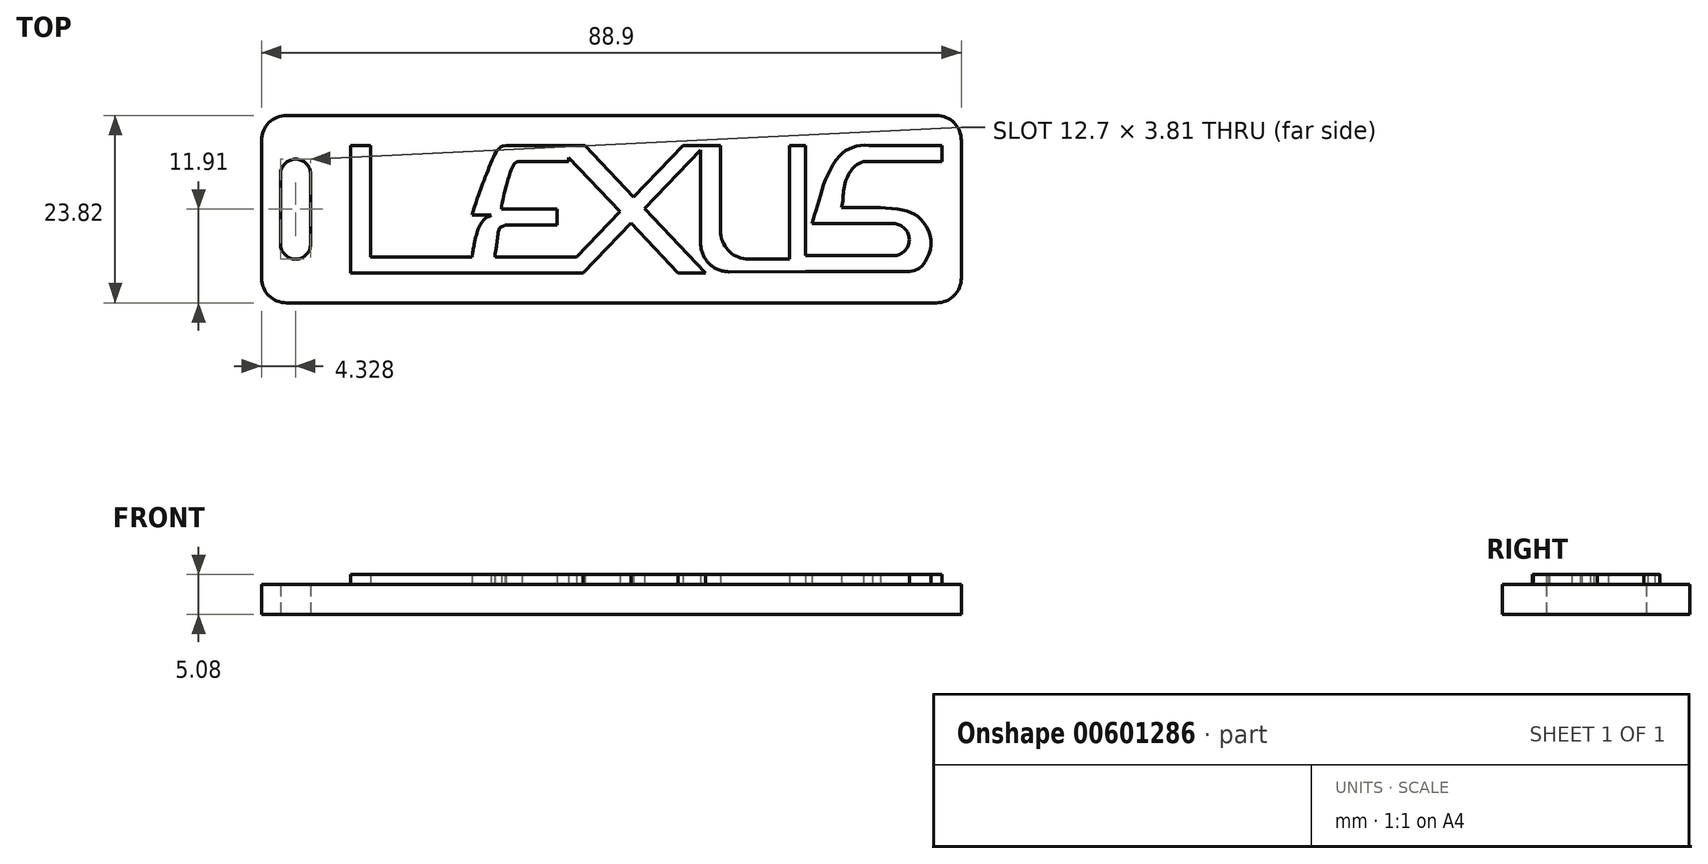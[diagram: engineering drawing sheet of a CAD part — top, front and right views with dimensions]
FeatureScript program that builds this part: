
annotation { "Feature Type Name" : "Feature", "Feature Type Description" : "" }
export const myFeature = defineFeature(function(context is Context, id is Id, definition is map)
    precondition{}
    {
        {
            var Q0;
            Q0=qCreatedBy(makeId("Top.planeOp"),FACE);
            var sketch = newSketch(context, id + "F0", { "sketchPlane" : qUnion([Q0])});
            skLineSegment(sketch, "E0.bottom", {"start": v(41.28, -11.9) * mm, "end": v(-41.28, -11.9) * mm});
            skLineSegment(sketch, "E0.top", {"start": v(41.28, 11.9) * mm, "end": v(-41.28, 11.9) * mm});
            skLineSegment(sketch, "E0.left", {"start": v(44.45, -8.73) * mm, "end": v(44.45, 8.73) * mm});
            skLineSegment(sketch, "E0.right", {"start": v(-44.45, -8.73) * mm, "end": v(-44.45, 8.73) * mm});
            skPoint(sketch, "E0.middle", {"position": v(0, 0) * mm});
            skPoint(sketch, "E1.visualSharp", {"position": v(-44.45, 11.9) * mm});
            skArc(sketch, "E1.filletArc", {"start": v(-41.28, 11.9) * mm, "mid": v(-43.52, 10.98) * mm, "end": v(-44.45, 8.73) * mm});
            skPoint(sketch, "E2.visualSharp", {"position": v(44.45, 11.9) * mm});
            skArc(sketch, "E2.filletArc", {"start": v(44.45, 8.73) * mm, "mid": v(43.52, 10.98) * mm, "end": v(41.28, 11.9) * mm});
            skPoint(sketch, "E3.visualSharp", {"position": v(44.45, -11.9) * mm});
            skArc(sketch, "E3.filletArc", {"start": v(41.28, -11.9) * mm, "mid": v(43.52, -10.98) * mm, "end": v(44.45, -8.73) * mm});
            skPoint(sketch, "E4.visualSharp", {"position": v(-44.45, -11.9) * mm});
            skArc(sketch, "E4.filletArc", {"start": v(-44.45, -8.73) * mm, "mid": v(-43.52, -10.98) * mm, "end": v(-41.28, -11.9) * mm});
            skLineSegment(sketch, "E5.bottom", {"start": v(-40.12, -6.35) * mm, "end": v(-40.12, -6.35) * mm});
            skLineSegment(sketch, "E5.top", {"start": v(-40.12, 6.35) * mm, "end": v(-40.12, 6.35) * mm});
            skLineSegment(sketch, "E5.left", {"start": v(-38.22, -4.45) * mm, "end": v(-38.22, 4.45) * mm});
            skLineSegment(sketch, "E5.right", {"start": v(-42.03, -4.45) * mm, "end": v(-42.03, 4.45) * mm});
            skPoint(sketch, "E5.middle", {"position": v(-40.12, 0) * mm});
            skPoint(sketch, "E6.visualSharp", {"position": v(-38.22, 6.35) * mm});
            skArc(sketch, "E6.filletArc", {"start": v(-38.22, 4.45) * mm, "mid": v(-38.77, 5.8) * mm, "end": v(-40.12, 6.35) * mm});
            skPoint(sketch, "E7.visualSharp", {"position": v(-42.03, 6.35) * mm});
            skArc(sketch, "E7.filletArc", {"start": v(-40.12, 6.35) * mm, "mid": v(-41.47, 5.8) * mm, "end": v(-42.03, 4.45) * mm});
            skPoint(sketch, "E8.visualSharp", {"position": v(-42.03, -6.35) * mm});
            skArc(sketch, "E8.filletArc", {"start": v(-42.03, -4.45) * mm, "mid": v(-41.47, -5.8) * mm, "end": v(-40.12, -6.35) * mm});
            skPoint(sketch, "E9.visualSharp", {"position": v(-38.22, -6.35) * mm});
            skArc(sketch, "E9.filletArc", {"start": v(-40.12, -6.35) * mm, "mid": v(-38.77, -5.8) * mm, "end": v(-38.22, -4.45) * mm});
            skSolve(sketch);
        }
        {
            var Q0;
            Q0=makeQuery(id+"F0.imprint","IMPRINT",FACE,{"disambiguationData":[TD([[makeQuery(id+"F0.imprint","IMPRINT",EDGE,{"derivedFrom":sQuery(id+"F0.wireOp",EDGE,"E0.bottom")}),-1.0]])]});
            extrude(context, id + "F1", {"entities" : qUnion([Q0]), "depth" : 3.8 * mm, "offsetDistance" : 25.4 * mm});
        }
        {
            var Q0;
            Q0=makeQuery(id+"F1.opExtrude","CAP_FACE",FACE,{"disambiguationData":[OSD([sQuery(id+"F0.wireOp",EDGE,"E0.bottom"),sQuery(id+"F0.wireOp",EDGE,"E0.top"),sQuery(id+"F0.wireOp",EDGE,"E0.left"),sQuery(id+"F0.wireOp",EDGE,"E0.right"),sQuery(id+"F0.wireOp",EDGE,"E1.filletArc"),sQuery(id+"F0.wireOp",EDGE,"E2.filletArc"),sQuery(id+"F0.wireOp",EDGE,"E3.filletArc"),sQuery(id+"F0.wireOp",EDGE,"E4.filletArc"),sQuery(id+"F0.wireOp",EDGE,"E5.left"),sQuery(id+"F0.wireOp",EDGE,"E5.right"),sQuery(id+"F0.wireOp",EDGE,"E6.filletArc"),sQuery(id+"F0.wireOp",EDGE,"E7.filletArc"),sQuery(id+"F0.wireOp",EDGE,"E8.filletArc"),sQuery(id+"F0.wireOp",EDGE,"E9.filletArc")])],"isStart":false});
            var sketch = newSketch(context, id + "F2", { "sketchPlane" : qUnion([Q0])});
            skLineSegment(sketch, "E10", {"start": v(-33.14, -8.1) * mm, "end": v(-33.14, 8.1) * mm});
            skLineSegment(sketch, "E11", {"start": v(-33.14, 8.1) * mm, "end": v(-30.6, 8.1) * mm});
            skLineSegment(sketch, "E12", {"start": v(-30.6, 8.1) * mm, "end": v(-30.6, -6.06) * mm});
            skLineSegment(sketch, "E13", {"start": v(-30.6, -6.06) * mm, "end": v(-17.69, -6.06) * mm});
            skLineSegment(sketch, "E14", {"start": v(-14.93, -8.1) * mm, "end": v(-33.14, -8.1) * mm});
            skLineSegment(sketch, "E15", {"start": v(-15.3, -0.76) * mm, "end": v(-17.69, -0.76) * mm});
            skFitSpline(sketch, "E16", {"points": [v(-17.69, -0.76) * mm, v(-16.6, 2.6) * mm, v(-15.9, 4.42) * mm, v(-15, 6.56) * mm, v(-14.35, 7.63) * mm, v(-13.4, 8.1) * mm], "startDerivative": vector(6.68, 22.76) * mm, "endDerivative": vector(10.34, 0.39) * mm});
            skLineSegment(sketch, "E17", {"start": v(-13.4, 8.1) * mm, "end": v(-5.41, 8.1) * mm});
            skLineSegment(sketch, "E18", {"start": v(-5.41, 8.1) * mm, "end": v(-5.41, 6.06) * mm});
            skLineSegment(sketch, "E19", {"start": v(-5.41, 6.06) * mm, "end": v(-11.37, 6.06) * mm});
            skLineSegment(sketch, "E20", {"start": v(-13.98, 0) * mm, "end": v(-6.88, 0) * mm});
            skLineSegment(sketch, "E21", {"start": v(-6.88, 0) * mm, "end": v(-6.88, -2.03) * mm});
            skLineSegment(sketch, "E22", {"start": v(-6.88, -2.03) * mm, "end": v(-13.51, -2.03) * mm});
            skFitSpline(sketch, "E23", {"points": [v(-11.37, 6.06) * mm, v(-12.28, 5.85) * mm, v(-12.92, 4.45) * mm, v(-13.37, 2.93) * mm, v(-13.98, 0) * mm], "startDerivative": vector(-6.84, 0.48) * mm, "endDerivative": vector(-1.14, -9.07) * mm});
            skFitSpline(sketch, "E24", {"points": [v(-17.69, -6.06) * mm, v(-17.48, -4.75) * mm, v(-17.16, -3.28) * mm, v(-16.77, -2.16) * mm, v(-16.14, -1.27) * mm, v(-15.3, -0.76) * mm], "startDerivative": vector(1.78, 14.07) * mm, "endDerivative": vector(7.84, 3.88) * mm});
            skFitSpline(sketch, "E25", {"points": [v(-13.51, -2.03) * mm, v(-14.2, -2.4) * mm, v(-14.5, -3.96) * mm, v(-14.71, -5.37) * mm, v(-14.77, -6.06) * mm], "startDerivative": vector(-4.95, -2.36) * mm, "endDerivative": vector(0.17, -4.54) * mm});
            skLineSegment(sketch, "E26", {"start": v(-14.93, -8.1) * mm, "end": v(-4.44, -8.1) * mm});
            skLineSegment(sketch, "E27", {"start": v(-4.44, -8.1) * mm, "end": v(-4.44, -6.06) * mm});
            skLineSegment(sketch, "E28", {"start": v(-4.44, -6.06) * mm, "end": v(-14.77, -6.06) * mm});
            skLineSegment(sketch, "E29", {"start": v(37.84, -7.94) * mm, "end": v(24.67, -7.94) * mm});
            skLineSegment(sketch, "E30", {"start": v(24.67, -5.9) * mm, "end": v(35.8, -5.9) * mm});
            skLineSegment(sketch, "E31", {"start": v(37.84, -3.88) * mm, "end": v(37.84, -3.88) * mm});
            skLineSegment(sketch, "E32", {"start": v(35.8, -1.84) * mm, "end": v(25.48, -1.84) * mm});
            skPoint(sketch, "E33.visualSharp", {"position": v(37.84, -1.84) * mm});
            skArc(sketch, "E33.filletArc", {"start": v(37.84, -3.88) * mm, "mid": v(37.24, -2.44) * mm, "end": v(35.8, -1.84) * mm});
            skPoint(sketch, "E34.visualSharp", {"position": v(37.84, -5.9) * mm});
            skArc(sketch, "E34.filletArc", {"start": v(35.8, -5.9) * mm, "mid": v(37.24, -5.31) * mm, "end": v(37.84, -3.88) * mm});
            skFitSpline(sketch, "E35", {"points": [v(37.84, -7.94) * mm, v(39.4, -7.3) * mm, v(40.12, -6.12) * mm, v(40.58, -4.82) * mm, v(40.45, -3.13) * mm, v(39.67, -1.7) * mm, v(38.76, -0.8) * mm, v(37.84, -0.34) * mm, v(36.42, 0) * mm, v(34.18, 0.19) * mm], "startDerivative": vector(16.67, 3.29) * mm, "endDerivative": vector(-12.35, -0.23) * mm});
            skLineSegment(sketch, "E36", {"start": v(34.18, 0.19) * mm, "end": v(29.24, 0.19) * mm});
            skFitSpline(sketch, "E37", {"points": [v(25.48, -1.84) * mm, v(26.05, 0) * mm, v(26.74, 2.45) * mm, v(27.79, 5) * mm, v(29.18, 6.97) * mm, v(30.34, 7.73) * mm, v(31.68, 8.1) * mm, v(33.19, 8.1) * mm], "startDerivative": vector(4.18, 16.22) * mm, "endDerivative": vector(10.2, 0.23) * mm});
            skLineSegment(sketch, "E38", {"start": v(33.19, 8.1) * mm, "end": v(41.96, 8.1) * mm});
            skLineSegment(sketch, "E39", {"start": v(41.96, 8.1) * mm, "end": v(41.96, 6.06) * mm});
            skLineSegment(sketch, "E40", {"start": v(41.96, 6.06) * mm, "end": v(32.02, 6.06) * mm});
            skFitSpline(sketch, "E41", {"points": [v(29.24, 0.19) * mm, v(29.53, 2.62) * mm, v(30.34, 4.77) * mm, v(32.02, 6.06) * mm], "startDerivative": vector(1.82, 6.68) * mm, "endDerivative": vector(7.78, 2.73) * mm});
            skLineSegment(sketch, "E42", {"start": v(-3.36, 8.1) * mm, "end": v(11.94, -8.1) * mm});
            skLineSegment(sketch, "E43", {"start": v(-3.36, 8.1) * mm, "end": v(-5.41, 8.1) * mm});
            skLineSegment(sketch, "E44", {"start": v(11.94, -8.1) * mm, "end": v(8.45, -8.1) * mm});
            skLineSegment(sketch, "E45", {"start": v(8.45, -8.1) * mm, "end": v(-5.41, 6.57) * mm});
            skLineSegment(sketch, "E46", {"start": v(14.94, -7.96) * mm, "end": v(24.67, -7.94) * mm});
            skLineSegment(sketch, "E47", {"start": v(24.67, -7.94) * mm, "end": v(24.67, 8.1) * mm});
            skLineSegment(sketch, "E48", {"start": v(24.67, 8.1) * mm, "end": v(22.64, 8.1) * mm});
            skLineSegment(sketch, "E49", {"start": v(22.64, 8.1) * mm, "end": v(22.64, -6.35) * mm});
            skLineSegment(sketch, "E50", {"start": v(22.64, -6.35) * mm, "end": v(17.43, -6.35) * mm});
            skArc(sketch, "E51.filletArc", {"start": v(13.89, -3.1) * mm, "mid": v(15.03, -5.41) * mm, "end": v(17.43, -6.35) * mm});
            skPoint(sketch, "E52.visualSharp", {"position": v(10.6, -7.96) * mm});
            skPoint(sketch, "E53.visualSharp", {"position": v(11.35, -7.96) * mm});
            skArc(sketch, "E53.filletArc", {"start": v(11.35, -4.37) * mm, "mid": v(12.4, -6.9) * mm, "end": v(14.94, -7.96) * mm});
            skLineSegment(sketch, "E54", {"start": v(-4.44, -8.1) * mm, "end": v(-3.57, -8.1) * mm});
            skLineSegment(sketch, "E55", {"start": v(-3.57, -8.1) * mm, "end": v(11.94, 8.1) * mm});
            skLineSegment(sketch, "E56", {"start": v(-4.44, -6.06) * mm, "end": v(9.13, 8.1) * mm});
            skLineSegment(sketch, "E57", {"start": v(9.13, 8.1) * mm, "end": v(11.94, 8.1) * mm});
            skLineSegment(sketch, "E58", {"start": v(11.35, -4.37) * mm, "end": v(11.35, 7.48) * mm});
            skLineSegment(sketch, "E59", {"start": v(11.35, 7.48) * mm, "end": v(11.94, 8.1) * mm});
            skLineSegment(sketch, "E60", {"start": v(13.89, -3.1) * mm, "end": v(13.89, 8.1) * mm});
            skLineSegment(sketch, "E61", {"start": v(13.89, 8.1) * mm, "end": v(11.94, 8.1) * mm});
            skSolve(sketch);
        }
        {
            var Q0;
            Q0 = qSketchRegion(id + "F2", true);
            extrude(context, id + "F3", {"entities" : qUnion([Q0]), "operationType" : NewBodyOperationType.ADD, "depth" : 1.27 * mm, "offsetDistance" : 25.4 * mm});
        }
    });
